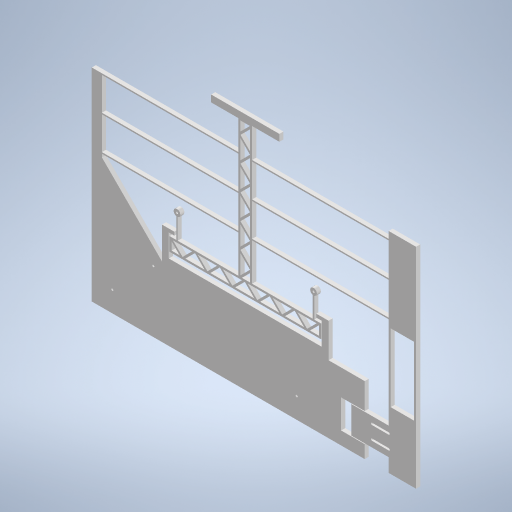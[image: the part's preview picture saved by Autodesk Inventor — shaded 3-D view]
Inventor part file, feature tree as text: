
AUTODESK INVENTOR PART (.ipt)
format: ipt  version: 2023 (Build 270158000, 158)  size: 688,640 bytes
history: native  units: mm
features: extrude x8, sketch x8, other x3, reference x2, projected_geometry x1
ambient origin geometry x8: Origin, YZ Plane, XZ Plane, XY Plane, X Axis, Y Axis, Z Axis, Center Point
bodies: Solid1 (feature_tree)
feature tree (22):
  extrude  "Extrusion1"  Depth=350.0mm
  extrude  "Extrusion2"  TaperAngle=45.0deg  [1 undecoded]
  extrude  "Extrusion3"  Depth=100.0mm
  extrude  "Extrusion4"  Depth=3.0mm
  extrude  "Extrusion6"  Depth=10.0mm
  extrude  "Extrusion7"  Depth=2.0mm
  extrude  "Extrusion8"  Depth=30.0mm
  extrude  "Extrusion5"  Depth=20.0mm
  sketch  "Sketch1"  dims[d0=420.0mm d1=350.0mm]
  sketch  "Sketch2"  dims[d2=45.0deg d3=45.0deg]
  reference  "Reference1"
  sketch  "Sketch3"  dims[d4=100.0mm d5=100.0mm]
  sketch  "Sketch4"  dims[d6=3.0mm d7=3.0mm]
  reference  "Reference2"
  sketch  "Sketch5"  dims[d8=10.0mm d9=10.0mm]
  projected_geometry  "Projected Loop1"
  sketch  "Sketch6"  dims[d10=1.0mm d11=2.0mm]
  sketch  "Sketch7"  dims[d12=30.0mm d13=30.0mm]
  sketch  "Sketch8"  dims[d14=2.0mm d15=20.0mm d16=10.0mm d17=10.0mm d23=10.0mm d24=10.0mm d25=10.0mm d26=200.0mm d28=2.0mm d29=200.0mm d30=2.0mm d31=200.0mm d32=100.0mm d33=20.0mm d34=10.0mm d35=40.0mm d36=40.0mm d37=200.0mm d38=200.0mm d39=2.0mm d40=2.0mm d41=100.0mm d42=2.0mm d43=50.0mm d44=40.0mm d45=10.0mm d46=10.0mm d47=50.0mm d48=100.0mm d49=3.0mm d50=3.0mm d52=6.0mm d53=0.0mm d54=1.0mm d55=1.0mm d56=40.0mm d57=15.0mm d58=20.0mm d59=6.0mm d60=0.0mm d61=45.0deg d62=6.0mm d63=0.0mm d64=6.0mm d65=0.0mm d66=9.0mm d67=10.0mm d68=0.0mm d69=2.0mm d70=475.0mm d71=6.0mm d72=0.0mm d73=30.0mm d74=20.0mm d75=3.0mm d76=3.0mm d77=40.0mm d78=30.0mm d79=3.0mm d80=3.0mm d81=30.0mm d82=30.0mm d83=6.0mm d84=0.0mm d85=3.0mm d86=3.0mm d87=3.0mm d88=3.0mm d89=3.0mm d90=1.5mm d91=45.0deg d92=3.0mm d93=3.0mm d94=36.485281mm d95=60.0mm d97=36.485281mm d98=10.0mm d100=10.0mm d102=3.0mm d103=3.0mm d104=3.0mm d105=3.0mm d106=3.0mm d107=1.5mm d108=45.0deg d109=3.0mm d110=3.0mm d111=36.485281mm d112=50.0mm d114=36.485281mm d115=10.0mm d117=10.0mm d119=10.0mm d120=0.0mm d121=0.0mm d122=0.0mm d123=10.0mm d124=10.0mm d125=1.0mm d126=1.0mm d127=5.0mm d128=4.0mm d129=5.0mm d130=3.0mm d131=3.0mm d132=4.0mm]
  other  "<userpath>\ClawdDrive\Objet3D\IminaProbe\RoueMDF\Assembly1.iam"
  other  "Assembly1.iam"
  other  "Wheel1:1"
note: 1 required parameter value undecoded (feature->parameter linkage not recoverable at this tier; creation-order binding heuristic only, values carry confidence <= 0.55)
